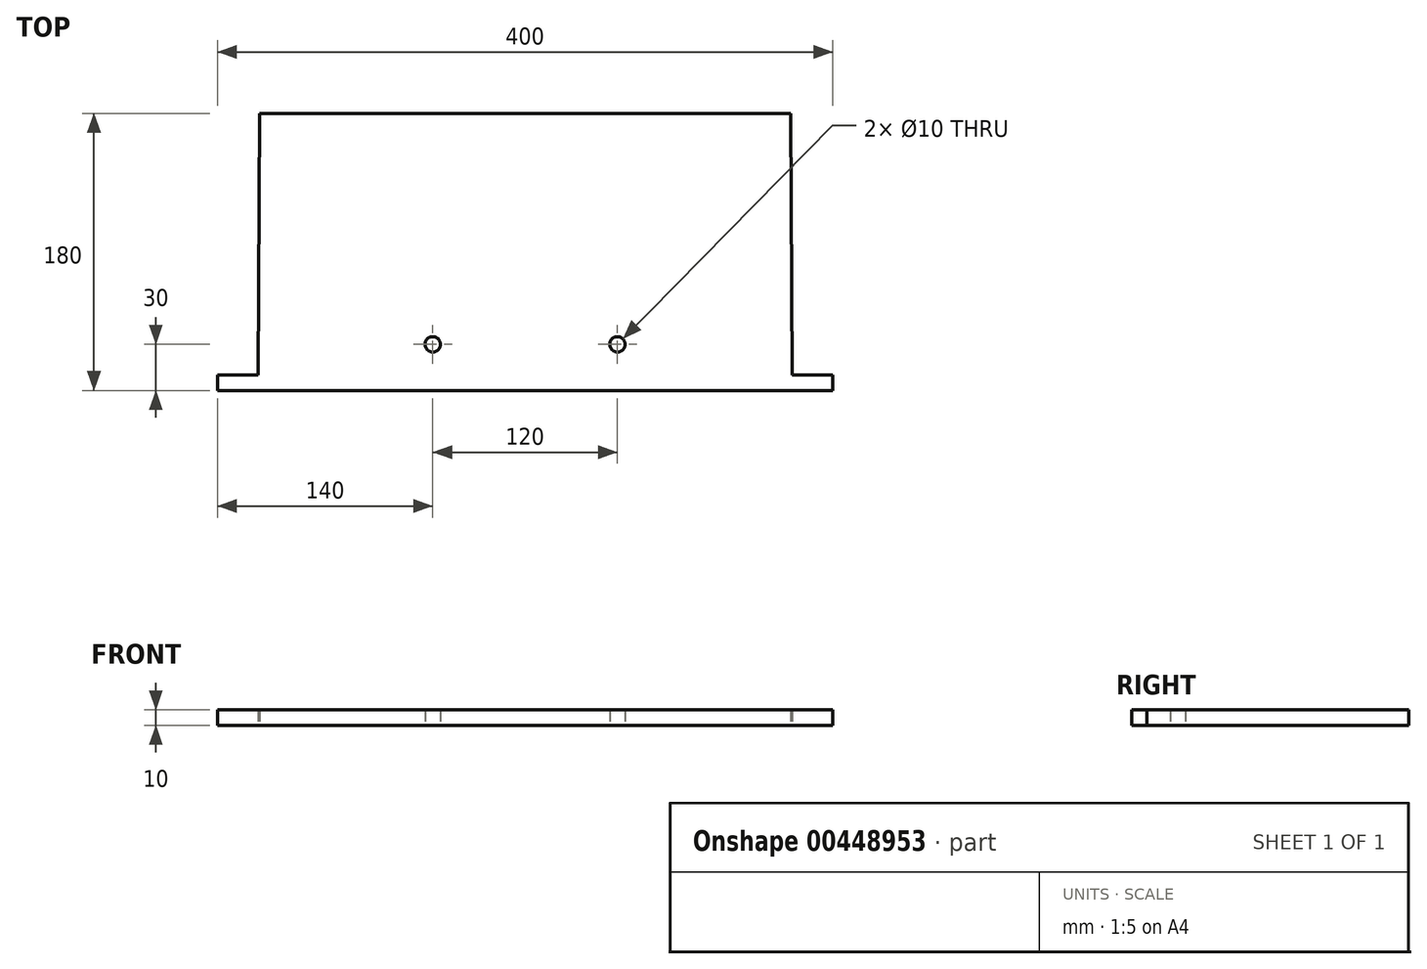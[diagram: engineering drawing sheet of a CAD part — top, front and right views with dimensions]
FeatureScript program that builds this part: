
annotation { "Feature Type Name" : "Feature", "Feature Type Description" : "" }
export const myFeature = defineFeature(function(context is Context, id is Id, definition is map)
    precondition{}
    {
        {
            var Q0;
            Q0=qCreatedBy(makeId("Top.planeOp"),FACE);
            var sketch = newSketch(context, id + "F0", { "sketchPlane" : qUnion([Q0])});
            skLineSegment(sketch, "E0.bottom", {"start": v(200, 90) * mm, "end": v(-200, 90) * mm});
            skLineSegment(sketch, "E0.top", {"start": v(200, -90) * mm, "end": v(-200, -90) * mm});
            skLineSegment(sketch, "E0.left", {"start": v(200, 90) * mm, "end": v(200, -90) * mm});
            skLineSegment(sketch, "E0.right", {"start": v(-200, 90) * mm, "end": v(-200, -90) * mm});
            skPoint(sketch, "E0.middle", {"position": v(0, 0) * mm});
            skLineSegment(sketch, "E1", {"start": v(-200, -90) * mm, "end": v(-200, -80) * mm});
            skLineSegment(sketch, "E2", {"start": v(-173.5, -80) * mm, "end": v(-200, -80) * mm});
            skLineSegment(sketch, "E3", {"start": v(-173.5, -80) * mm, "end": v(-172.5, 90) * mm});
            skLineSegment(sketch, "E4", {"start": v(-172.5, 90) * mm, "end": v(172.5, 90) * mm});
            skLineSegment(sketch, "E5", {"start": v(172.5, 90) * mm, "end": v(173.5, -80) * mm});
            skLineSegment(sketch, "E6", {"start": v(173.5, -80) * mm, "end": v(200, -80) * mm});
            skLineSegment(sketch, "E7.bottom", {"start": v(60, -60) * mm, "end": v(-60, -60) * mm});
            skLineSegment(sketch, "E7.top", {"start": v(60, 60) * mm, "end": v(-60, 60) * mm});
            skLineSegment(sketch, "E7.left", {"start": v(60, -60) * mm, "end": v(60, 60) * mm});
            skLineSegment(sketch, "E7.right", {"start": v(-60, -60) * mm, "end": v(-60, 60) * mm});
            skCircle(sketch, "E8", {"center": v(60, -60) * mm, "radius": 5 * mm});
            skCircle(sketch, "E9", {"center": v(-60, -60) * mm, "radius": 5 * mm});
            skSolve(sketch);
        }
        {
            var Q0;
            {var subQ6=sQuery(id+"F0.wireOp",EDGE,"E0.top");Q0=makeQuery(id+"F0.imprint","IMPRINT",FACE,{"disambiguationData":[TD([[makeQuery(id+"F0.imprint","IMPRINT",EDGE,{"derivedFrom":subQ6}),-1.0]])]});}
            var Q1;
            {var subQ1=sQuery(id+"F0.wireOp",EDGE,"E7.top");Q1=makeQuery(id+"F0.imprint","IMPRINT",FACE,{"disambiguationData":[TD([[makeQuery(id+"F0.imprint","IMPRINT",EDGE,{"derivedFrom":subQ1}),1.0]])]});}
            extrude(context, id + "F1", {"entities" : qUnion([Q0, Q1]), "depth" : 10 * mm});
        }
    });
